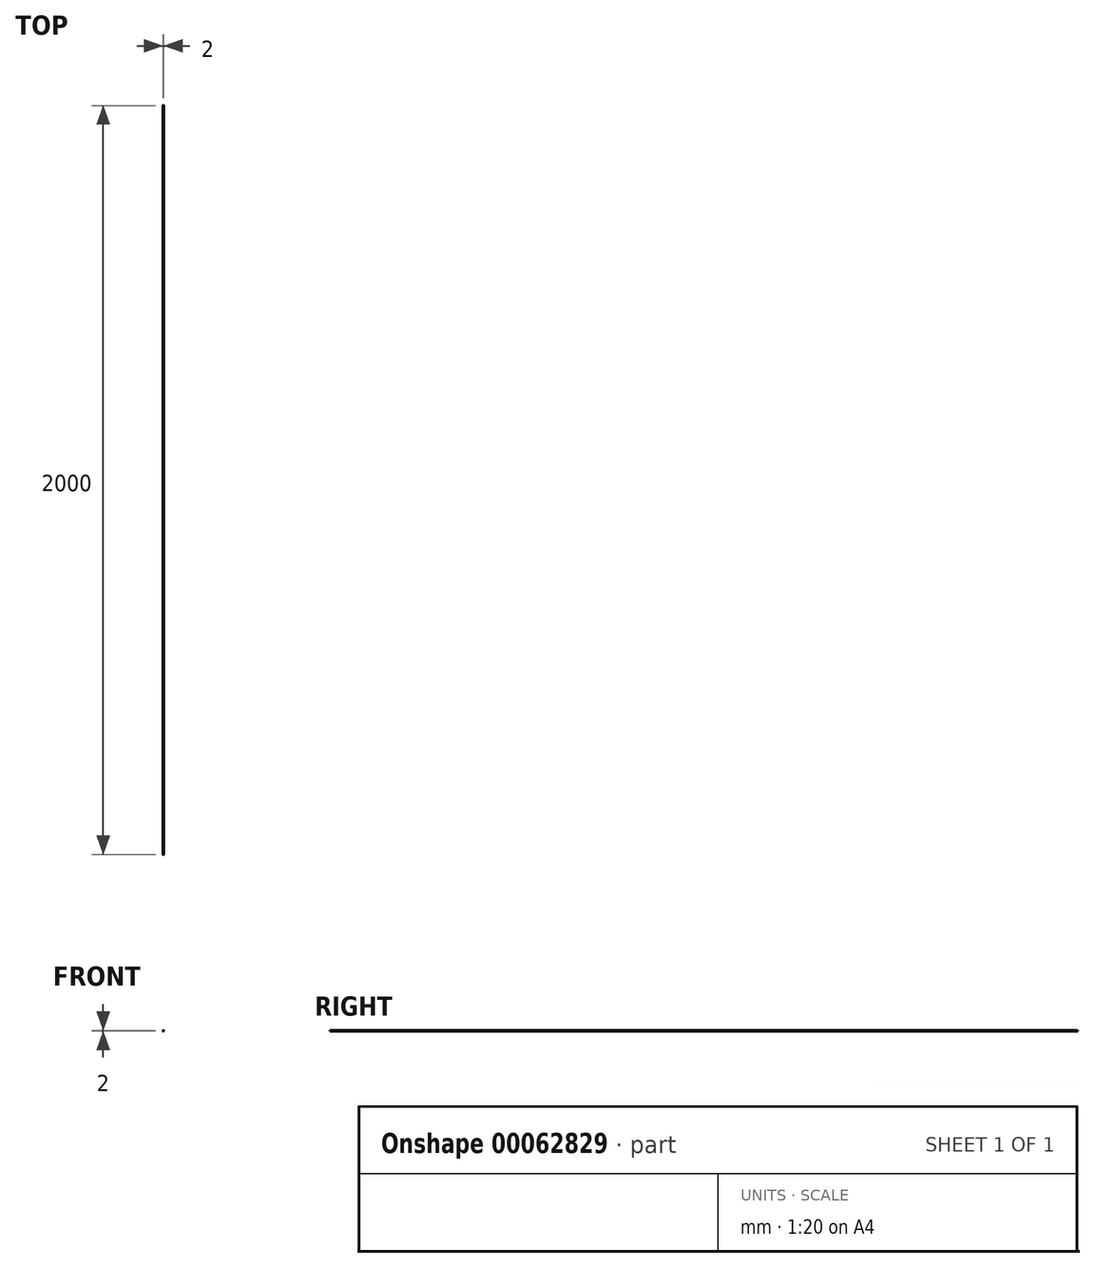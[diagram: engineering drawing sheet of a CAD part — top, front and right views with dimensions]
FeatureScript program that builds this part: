
annotation { "Feature Type Name" : "Feature", "Feature Type Description" : "" }
export const myFeature = defineFeature(function(context is Context, id is Id, definition is map)
    precondition{}
    {
        {
            var Q0;
            Q0=qCreatedBy(makeId("Front.planeOp"),FACE);
            var sketch = newSketch(context, id + "F0", { "sketchPlane" : qUnion([Q0])});
            skCircle(sketch, "E0", {"center": v(0, 0) * mm, "radius": 1 * mm});
            skSolve(sketch);
        }
        {
            var Q0;
            Q0 = qSketchRegion(id + "F0", true);
            extrude(context, id + "F1", {"entities" : qUnion([Q0]), "depth" : 2000 * mm});
        }
    });
